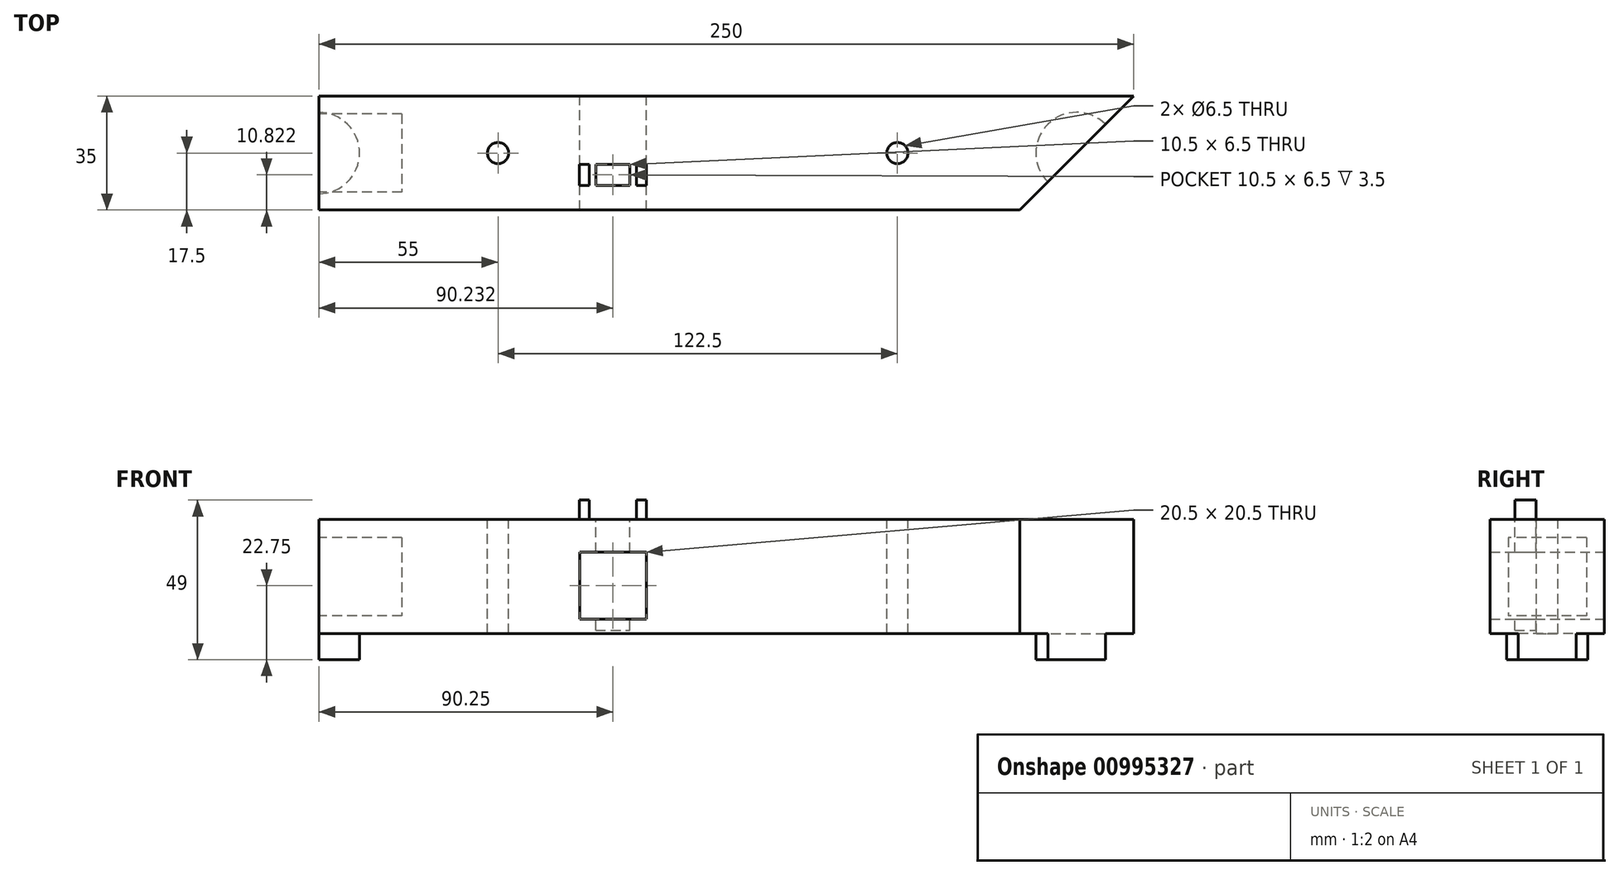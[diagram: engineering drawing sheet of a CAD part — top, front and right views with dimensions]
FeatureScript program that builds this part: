
annotation { "Feature Type Name" : "Feature", "Feature Type Description" : "" }
export const myFeature = defineFeature(function(context is Context, id is Id, definition is map)
    precondition{}
    {
        {
            var Q0;
            Q0=qCreatedBy(makeId("Top.planeOp"),FACE);
            var sketch = newSketch(context, id + "F0", { "sketchPlane" : qUnion([Q0])});
            skLineSegment(sketch, "E0.bottom", {"start": v(125, 17.5) * mm, "end": v(-125, 17.5) * mm});
            skLineSegment(sketch, "E0.top", {"start": v(90, -17.5) * mm, "end": v(-125, -17.5) * mm});
            skLineSegment(sketch, "E0.right", {"start": v(-125, 17.5) * mm, "end": v(-125, -17.5) * mm});
            skPoint(sketch, "E0.middle", {"position": v(0, 0) * mm});
            skPoint(sketch, "E1", {"position": v(90, -17.5) * mm});
            skLineSegment(sketch, "E2", {"start": v(125, 17.5) * mm, "end": v(90, -17.5) * mm});
            skPoint(sketch, "E3.orphan", {"position": v(125, -17.5) * mm});
            skSolve(sketch);
        }
        {
            var Q0;
            Q0=makeQuery(id+"F0.imprint","IMPRINT",FACE,{"disambiguationData":[TD([[makeQuery(id+"F0.imprint","IMPRINT",EDGE,{"derivedFrom":sQuery(id+"F0.wireOp",EDGE,"E0.bottom")}),1.0]])]});
            extrude(context, id + "F1", {"entities" : qUnion([Q0]), "depth" : 35 * mm, "offsetDistance" : 25 * mm});
        }
        {
            var Q0;
            Q0=makeQuery(id+"F1.opExtrude","CAP_FACE",FACE,{"disambiguationData":[OSD([sQuery(id+"F0.wireOp",EDGE,"E0.bottom"),sQuery(id+"F0.wireOp",EDGE,"E0.top"),sQuery(id+"F0.wireOp",EDGE,"E0.right"),sQuery(id+"F0.wireOp",EDGE,"E2")])],"isStart":false});
            var sketch = newSketch(context, id + "F2", { "sketchPlane" : qUnion([Q0])});
            skPoint(sketch, "E4", {"position": v(52.5, 0) * mm});
            skPoint(sketch, "E5", {"position": v(107.5, 0) * mm});
            skPoint(sketch, "E6", {"position": v(-70, 0) * mm});
            skPoint(sketch, "E7", {"position": v(-125, 0) * mm});
            skSolve(sketch);
        }
        {
            var Q0;
            Q0=sQuery(id+"F2.wireOp",VERTEX,"E6");
            var Q1;
            Q1=makeQuery(id+"F1.opExtrude","SWEPT_BODY",BODY,{"disambiguationData":[OSD([sQuery(id+"F0.wireOp",EDGE,"E0.bottom"),sQuery(id+"F0.wireOp",EDGE,"E0.top"),sQuery(id+"F0.wireOp",EDGE,"E0.right"),sQuery(id+"F0.wireOp",EDGE,"E2")])]});
            hole(context, id + "F3", {"style" : HoleStyle.SIMPLE, "endStyle" : HoleEndStyle.BLIND, "holeDiameter" : 6.5 * mm, "majorDiameter" : 5 * mm, "holeDepth" : 35 * mm, "isTappedThrough" : true, "tappedDepth" : 12 * mm, "tapClearance" : 3, "locations" : qUnion([Q0]), "scope" : qUnion([Q1])});
        }
        {
            var Q0;
            Q0=sQuery(id+"F2.wireOp",VERTEX,"E4");
            var Q1;
            Q1=makeQuery(id+"F1.opExtrude","SWEPT_BODY",BODY,{"disambiguationData":[OSD([sQuery(id+"F0.wireOp",EDGE,"E0.bottom"),sQuery(id+"F0.wireOp",EDGE,"E0.top"),sQuery(id+"F0.wireOp",EDGE,"E0.right"),sQuery(id+"F0.wireOp",EDGE,"E2")])]});
            hole(context, id + "F4", {"style" : HoleStyle.SIMPLE, "endStyle" : HoleEndStyle.BLIND, "holeDiameter" : 6.5 * mm, "majorDiameter" : 5 * mm, "holeDepth" : 35 * mm, "isTappedThrough" : true, "tappedDepth" : 12 * mm, "tapClearance" : 3, "locations" : qUnion([Q0]), "scope" : qUnion([Q1])});
        }
        {
            var Q0;
            Q0=makeQuery(id+"F1.opExtrude","SWEPT_FACE",FACE,{"disambiguationData":[OSD([sQuery(id+"F0.wireOp",EDGE,"E0.right")])]});
            var sketch = newSketch(context, id + "F5", { "sketchPlane" : qUnion([Q0])});
            skSolve(sketch);
        }
        {
            var Q0;
            {var subQ0=sQuery(id+"F0.wireOp",EDGE,"E0.right");Q0=makeQuery(id+"F5.imprint","IMPRINT",FACE,{"disambiguationData":[TD([[makeQuery(id+"F5.imprint","IMPRINT",EDGE,{"derivedFrom":makeQuery(id+"F1.opExtrude","CAP_EDGE",EDGE,{"disambiguationData":[OSD([subQ0])],"isStart":true})}),1.0]])]});}
            var sketch = newSketch(context, id + "F6", { "sketchPlane" : qUnion([Q0])});
            skLineSegment(sketch, "E8.0", {"start": v(-12, 5.5) * mm, "end": v(12, 5.5) * mm});
            skLineSegment(sketch, "E8.1", {"start": v(-12, 29.5) * mm, "end": v(-12, 5.5) * mm});
            skLineSegment(sketch, "E9.0", {"start": v(12, 29.5) * mm, "end": v(12, 5.5) * mm});
            skLineSegment(sketch, "E9.1", {"start": v(-12, 29.5) * mm, "end": v(12, 29.5) * mm});
            skSolve(sketch);
        }
        {
            var Q0;
            Q0=makeQuery(id+"F6.imprint","IMPRINT",FACE,{"disambiguationData":[TD([[makeQuery(id+"F6.imprint","IMPRINT",EDGE,{"derivedFrom":sQuery(id+"F6.wireOp",EDGE,"E8.0")}),1.0]])]});
            extrude(context, id + "F7", {"entities" : qUnion([Q0]), "operationType" : NewBodyOperationType.REMOVE, "oppositeDirection" : true, "depth" : 25.5 * mm, "offsetDistance" : 25 * mm});
        }
        {
            var Q0;
            Q0=makeQuery(id+"F1.opExtrude","CAP_FACE",FACE,{"disambiguationData":[OSD([sQuery(id+"F0.wireOp",EDGE,"E0.bottom"),sQuery(id+"F0.wireOp",EDGE,"E0.top"),sQuery(id+"F0.wireOp",EDGE,"E0.right"),sQuery(id+"F0.wireOp",EDGE,"E2")])],"isStart":true});
            var sketch = newSketch(context, id + "F8", { "sketchPlane" : qUnion([Q0])});
            skPoint(sketch, "E10", {"position": v(107.5, 0) * mm});
            skCircle(sketch, "E11", {"center": v(107.5, 0) * mm, "radius": 12.5 * mm});
            skSolve(sketch);
        }
        {
            var Q0;
            {var subQ0=sQuery(id+"F8.wireOp",EDGE,"E11");var subQ1=makeQuery(id+"F1.opExtrude","CAP_EDGE",EDGE,{"disambiguationData":[OSD([sQuery(id+"F0.wireOp",EDGE,"E2")])],"isStart":true});var subQ2=makeQuery(id+"F8.imprint","INTERSECT",VERTEX,{"disambiguationData":[OD(0.0)],"derivedFrom":[subQ1,subQ0]});Q0=makeQuery(id+"F8.imprint","IMPRINT",FACE,{"disambiguationData":[TD([[makeQuery(id+"F8.imprint","IMPRINT",EDGE,{"disambiguationData":[TD([[subQ2,1.0]])],"derivedFrom":subQ0}),1.0]])]});}
            extrude(context, id + "F9", {"entities" : qUnion([Q0]), "operationType" : NewBodyOperationType.ADD, "depth" : 8 * mm, "offsetDistance" : 25 * mm});
        }
        {
            var Q0;
            Q0=makeQuery(id+"F1.opExtrude","CAP_FACE",FACE,{"disambiguationData":[OSD([sQuery(id+"F0.wireOp",EDGE,"E0.bottom"),sQuery(id+"F0.wireOp",EDGE,"E0.top"),sQuery(id+"F0.wireOp",EDGE,"E0.right"),sQuery(id+"F0.wireOp",EDGE,"E2")])],"isStart":true});
            var sketch = newSketch(context, id + "F10", { "sketchPlane" : qUnion([Q0])});
            skCircle(sketch, "E12", {"center": v(-125, 0) * mm, "radius": 12.5 * mm});
            skSolve(sketch);
        }
        {
            var Q0;
            {var subQ0=sQuery(id+"F10.wireOp",EDGE,"E12");var subQ1=makeQuery(id+"F1.opExtrude","CAP_EDGE",EDGE,{"disambiguationData":[OSD([sQuery(id+"F0.wireOp",EDGE,"E0.right")])],"isStart":true});var subQ2=makeQuery(id+"F10.imprint","INTERSECT",VERTEX,{"disambiguationData":[OD(0.0)],"derivedFrom":[subQ1,subQ0]});Q0=makeQuery(id+"F10.imprint","IMPRINT",FACE,{"disambiguationData":[TD([[makeQuery(id+"F10.imprint","IMPRINT",EDGE,{"disambiguationData":[TD([[subQ2,-1.0]])],"derivedFrom":subQ0}),1.0]])]});}
            extrude(context, id + "F11", {"entities" : qUnion([Q0]), "operationType" : NewBodyOperationType.ADD, "depth" : 8 * mm, "offsetDistance" : 25 * mm});
        }
        {
            var Q0;
            Q0=makeQuery(id+"F1.opExtrude","SWEPT_FACE",FACE,{"disambiguationData":[OSD([sQuery(id+"F0.wireOp",EDGE,"E0.bottom")])]});
            var sketch = newSketch(context, id + "F12", { "sketchPlane" : qUnion([Q0])});
            skPoint(sketch, "E13", {"position": v(45, 25) * mm});
            skLineSegment(sketch, "E14.bottom", {"start": v(45, 25) * mm, "end": v(24.5, 25) * mm});
            skLineSegment(sketch, "E14.top", {"start": v(45, 4.5) * mm, "end": v(24.5, 4.5) * mm});
            skLineSegment(sketch, "E14.left", {"start": v(45, 25) * mm, "end": v(45, 4.5) * mm});
            skLineSegment(sketch, "E14.right", {"start": v(24.5, 25) * mm, "end": v(24.5, 4.5) * mm});
            skPoint(sketch, "E15", {"position": v(24.5, 35) * mm});
            skPoint(sketch, "E16", {"position": v(45, 35) * mm});
            skSolve(sketch);
        }
        {
            var Q0;
            Q0=makeQuery(id+"F12.imprint","IMPRINT",FACE,{"disambiguationData":[TD([[makeQuery(id+"F12.imprint","IMPRINT",EDGE,{"derivedFrom":sQuery(id+"F12.wireOp",EDGE,"E14.bottom")}),1.0]])]});
            var Q1;
            Q1=sQuery(id+"F12.wireOp",EDGE,"E14.bottom");
            extrude(context, id + "F13", {"entities" : qUnion([Q0]), "operationType" : NewBodyOperationType.REMOVE, "surfaceEntities" : qUnion([Q1]), "oppositeDirection" : true, "depth" : 100 * mm, "offsetDistance" : 25 * mm});
        }
        {
            var Q0;
            Q0=makeQuery(id+"F1.opExtrude","CAP_FACE",FACE,{"disambiguationData":[OSD([sQuery(id+"F0.wireOp",EDGE,"E0.bottom"),sQuery(id+"F0.wireOp",EDGE,"E0.top"),sQuery(id+"F0.wireOp",EDGE,"E0.right"),sQuery(id+"F0.wireOp",EDGE,"E2")])],"isStart":false});
            var sketch = newSketch(context, id + "F14", { "sketchPlane" : qUnion([Q0])});
            skPoint(sketch, "E17", {"position": v(-16.28, 97.92) * mm});
            skPoint(sketch, "E18", {"position": v(-24.54, 17.5) * mm});
            skPoint(sketch, "E19", {"position": v(-8.69, 103.63) * mm});
            skPoint(sketch, "E20", {"position": v(-45, 17.5) * mm});
            skPoint(sketch, "E21", {"position": v(17.73, 139.2) * mm});
            skPoint(sketch, "E22", {"position": v(-71.08, 32.76) * mm});
            skPoint(sketch, "E23", {"position": v(-45, -9.93) * mm});
            skPoint(sketch, "E24", {"position": v(-24.54, -9.93) * mm});
            skPoint(sketch, "E25", {"position": v(-45, 59.26) * mm});
            skLineSegment(sketch, "E26", {"start": v(-45, -9.93) * mm, "end": v(-24.54, -9.93) * mm});
            skPoint(sketch, "E27", {"position": v(-34.77, -9.93) * mm});
            skPoint(sketch, "E28", {"position": v(-15.54, 62.05) * mm});
            skPoint(sketch, "E29", {"position": v(-29.52, -9.93) * mm});
            skPoint(sketch, "E30", {"position": v(-40.02, -9.93) * mm});
            skLineSegment(sketch, "E31.bottom", {"start": v(-29.52, -9.93) * mm, "end": v(-40.02, -9.93) * mm});
            skLineSegment(sketch, "E31.top", {"start": v(-29.52, -3.43) * mm, "end": v(-40.02, -3.43) * mm});
            skLineSegment(sketch, "E31.left", {"start": v(-29.52, -9.93) * mm, "end": v(-29.52, -3.43) * mm});
            skLineSegment(sketch, "E31.right", {"start": v(-40.02, -9.93) * mm, "end": v(-40.02, -3.43) * mm});
            skSolve(sketch);
        }
        {
            var Q0;
            Q0=makeQuery(id+"F14.imprint","IMPRINT",FACE,{"disambiguationData":[TD([[makeQuery(id+"F14.imprint","IMPRINT",EDGE,{"derivedFrom":sQuery(id+"F14.wireOp",EDGE,"E31.top")}),1.0]])]});
            extrude(context, id + "F15", {"entities" : qUnion([Q0]), "operationType" : NewBodyOperationType.REMOVE, "oppositeDirection" : true, "depth" : 34 * mm, "offsetDistance" : 25 * mm});
        }
        {
            var Q0;
            Q0=makeQuery(id+"F1.opExtrude","CAP_FACE",FACE,{"disambiguationData":[OSD([sQuery(id+"F0.wireOp",EDGE,"E0.bottom"),sQuery(id+"F0.wireOp",EDGE,"E0.top"),sQuery(id+"F0.wireOp",EDGE,"E0.right"),sQuery(id+"F0.wireOp",EDGE,"E2")])],"isStart":false});
            var sketch = newSketch(context, id + "F16", { "sketchPlane" : qUnion([Q0])});
            skPoint(sketch, "E32", {"position": v(-27.52, -3.43) * mm});
            skPoint(sketch, "E33", {"position": v(-24.52, -9.93) * mm});
            skPoint(sketch, "E34", {"position": v(-45.02, -9.93) * mm});
            skPoint(sketch, "E35", {"position": v(-42.02, -3.43) * mm});
            skLineSegment(sketch, "E36.bottom", {"start": v(-45.02, -9.93) * mm, "end": v(-42.02, -9.93) * mm});
            skLineSegment(sketch, "E36.top", {"start": v(-45.02, -3.43) * mm, "end": v(-42.02, -3.43) * mm});
            skLineSegment(sketch, "E36.left", {"start": v(-45.02, -9.93) * mm, "end": v(-45.02, -3.43) * mm});
            skLineSegment(sketch, "E36.right", {"start": v(-42.02, -9.93) * mm, "end": v(-42.02, -3.43) * mm});
            skLineSegment(sketch, "E37.bottom", {"start": v(-27.52, -3.43) * mm, "end": v(-24.52, -3.43) * mm});
            skLineSegment(sketch, "E37.top", {"start": v(-27.52, -9.93) * mm, "end": v(-24.52, -9.93) * mm});
            skLineSegment(sketch, "E37.left", {"start": v(-27.52, -3.43) * mm, "end": v(-27.52, -9.93) * mm});
            skLineSegment(sketch, "E37.right", {"start": v(-24.52, -3.43) * mm, "end": v(-24.52, -9.93) * mm});
            skSolve(sketch);
        }
        {
            var Q0;
            Q0 = qSketchRegion(id + "F16", true);
            extrude(context, id + "F17", {"entities" : qUnion([Q0]), "operationType" : NewBodyOperationType.ADD, "depth" : 6 * mm, "offsetDistance" : 25 * mm});
        }
    });
